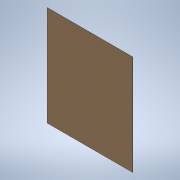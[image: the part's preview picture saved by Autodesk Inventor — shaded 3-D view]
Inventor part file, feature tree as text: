
AUTODESK INVENTOR PART (.ipt)
format: ipt  version: 2022 (Build 260153000, 153)  size: 111,104 bytes
history: native  units: mm
features: other x1, extrude x1, sketch x1
ambient origin geometry x8: Origin, YZ Plane, XZ Plane, XY Plane, X Axis, Y Axis, Z Axis, Center Point
bodies: Body1 (feature_tree)
feature tree (3):
  other  "Sólido1"
  extrude  "Extrusão1"  Depth=700.0mm
  sketch  "Esboço1"  dims[d0=600.0mm d1=700.0mm d2=3.0mm d3=0.0mm]
